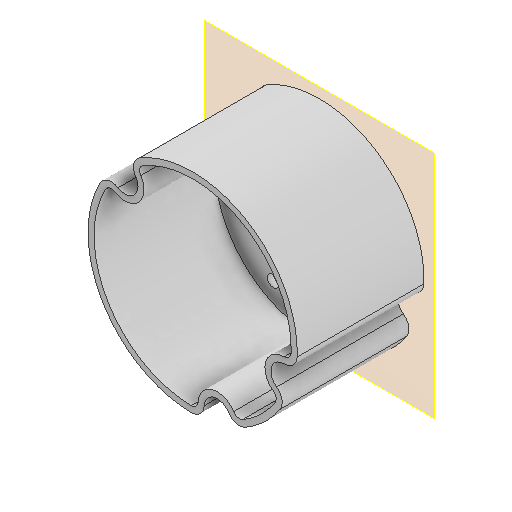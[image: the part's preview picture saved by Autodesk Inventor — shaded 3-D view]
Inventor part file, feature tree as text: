
AUTODESK INVENTOR PART (.ipt)
format: ipt  version: 2022 (Build 260153000, 153)  size: 212,992 bytes
history: native  units: mm
features: extrude x2, sketch x2, other x2, plane x1, reference x1, projected_geometry x1
ambient origin geometry x8: Origin, YZ Plane, XZ Plane, XY Plane, X Axis, Y Axis, Z Axis, Center Point
bodies: Volumenkörper1 (feature_tree)
feature tree (9):
  plane  "Arbeitsebene1"
  extrude  "Extrusion1"  Depth=2.8mm
  extrude  "Extrusion2"  Depth=30.0mm
  sketch  "Skizze1"  dims[d0=2.8mm d1=2.8mm]
  reference  "Referenz1"
  sketch  "Skizze2"  dims[d2=2.8mm d3=2.8mm d4=1.5mm d5=0.0mm d6=1.5mm d7=30.0mm d8=0.0mm]
  projected_geometry  "Projizierte Kontur1"
  other  "Anglerfish_bonne_mamman_m12large_v0.iam"
  other  "Anglerfish_bottom_v0:1"
